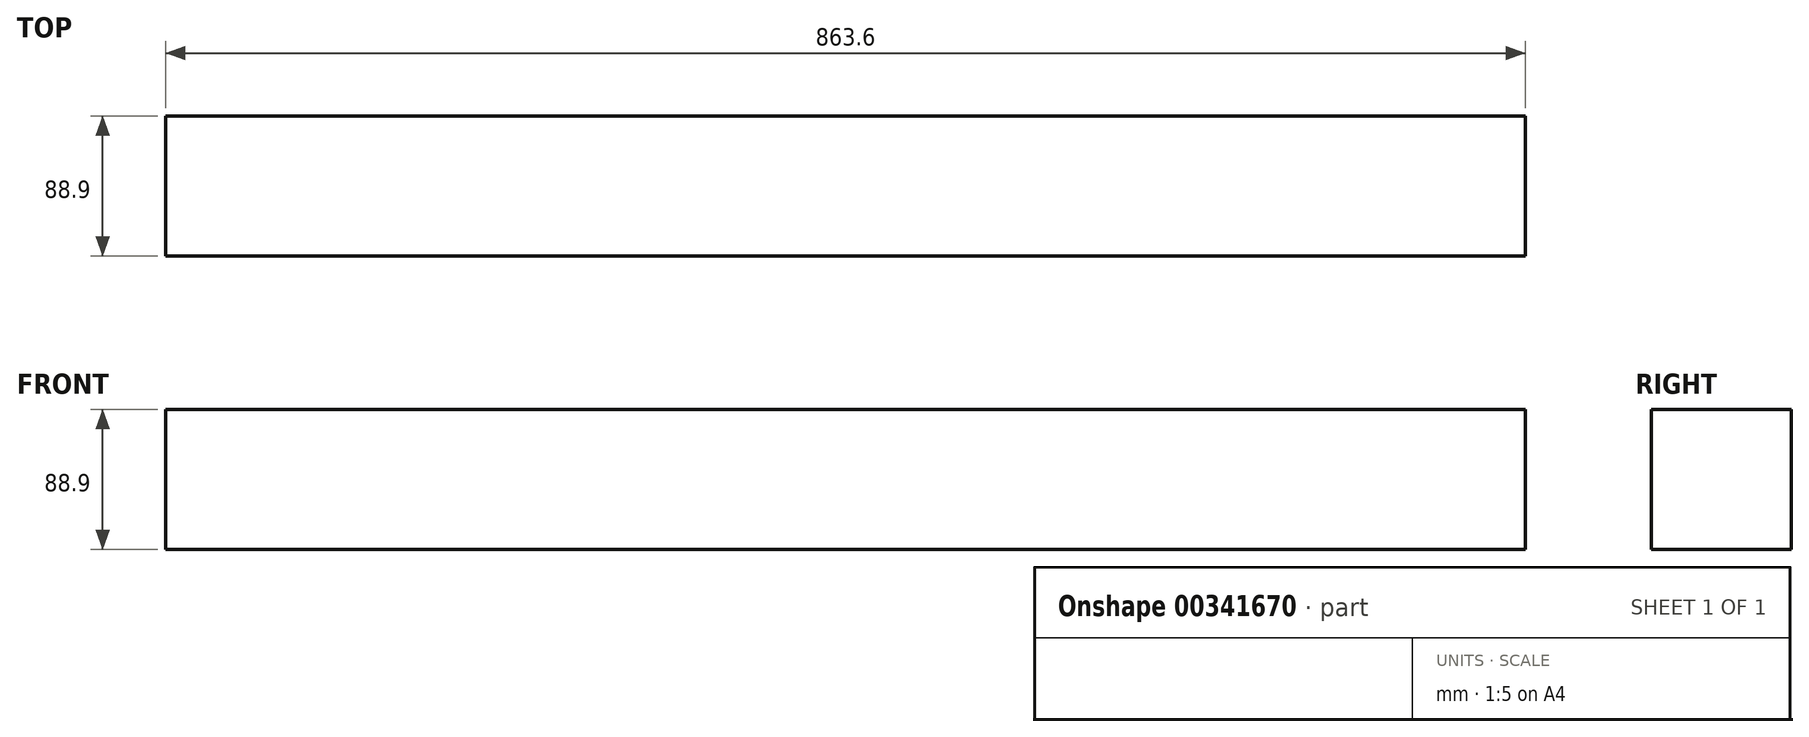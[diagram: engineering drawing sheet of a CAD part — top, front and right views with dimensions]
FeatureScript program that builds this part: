
annotation { "Feature Type Name" : "Feature", "Feature Type Description" : "" }
export const myFeature = defineFeature(function(context is Context, id is Id, definition is map)
    precondition{}
    {
        {
            var Q0;
            Q0=qCreatedBy(makeId("Front.planeOp"),FACE);
            var sketch = newSketch(context, id + "F0", { "sketchPlane" : qUnion([Q0])});
            skLineSegment(sketch, "E0.bottom", {"start": v(418.13, 53.83) * mm, "end": v(-445.47, 53.83) * mm});
            skLineSegment(sketch, "E0.top", {"start": v(418.13, -35.07) * mm, "end": v(-445.47, -35.07) * mm});
            skLineSegment(sketch, "E0.left", {"start": v(418.13, 53.83) * mm, "end": v(418.13, -35.07) * mm});
            skLineSegment(sketch, "E0.right", {"start": v(-445.47, 53.83) * mm, "end": v(-445.47, -35.07) * mm});
            skSolve(sketch);
        }
        {
            var Q0;
            Q0=makeQuery(id+"F0.imprint","IMPRINT",FACE,{"disambiguationData":[TD([[makeQuery(id+"F0.imprint","IMPRINT",EDGE,{"derivedFrom":sQuery(id+"F0.wireOp",EDGE,"E0.bottom")}),1.0]])]});
            extrude(context, id + "F1", {"entities" : qUnion([Q0]), "depth" : 88.9 * mm});
        }
    });
